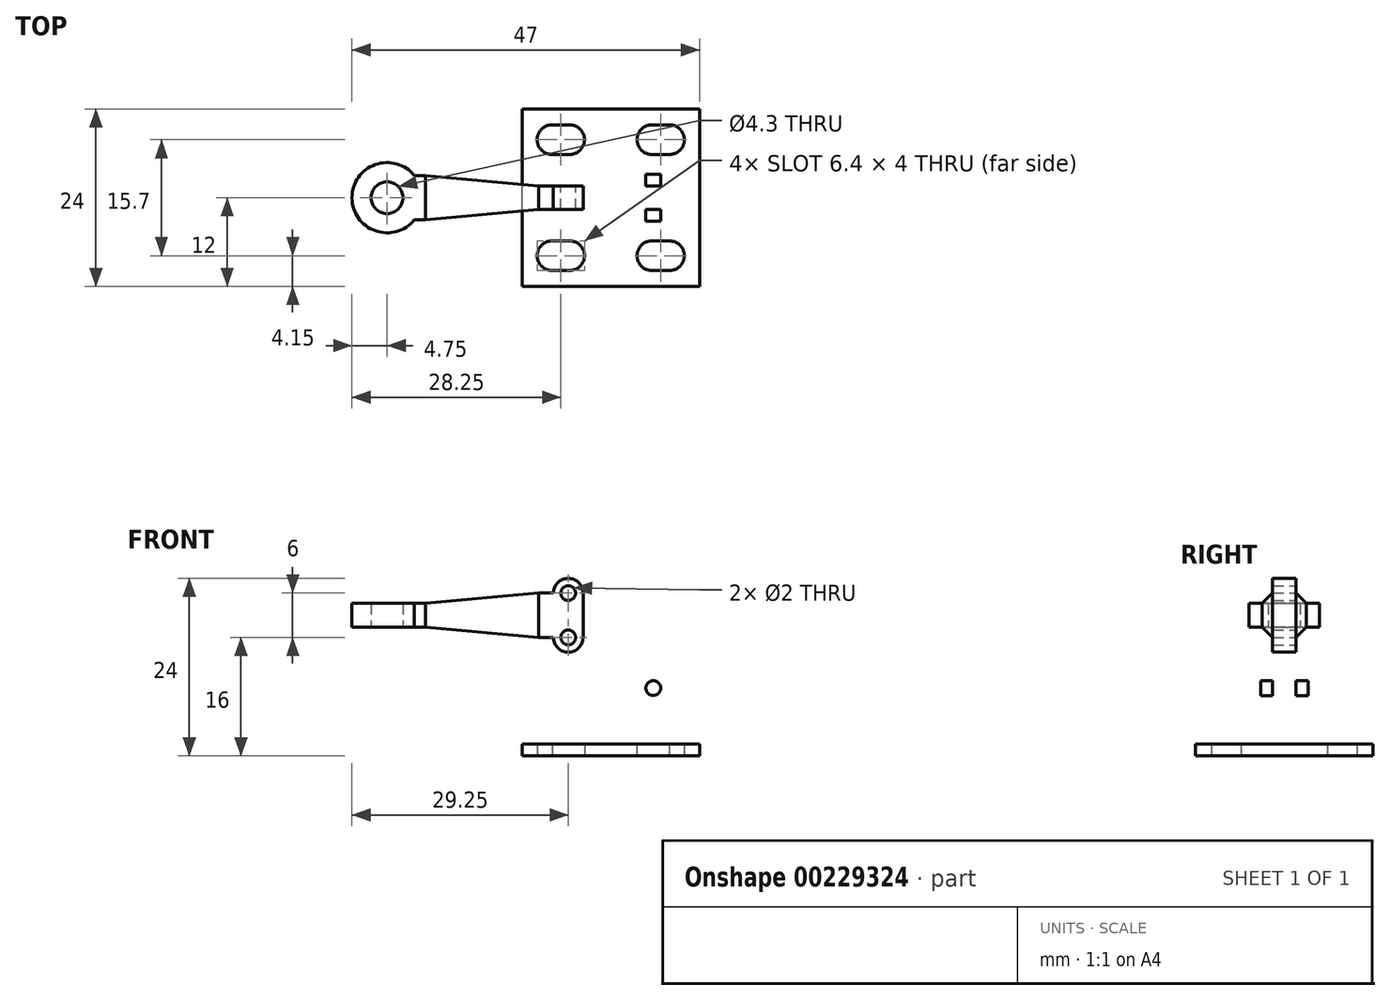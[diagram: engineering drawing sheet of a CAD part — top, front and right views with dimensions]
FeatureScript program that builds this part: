
annotation { "Feature Type Name" : "Feature", "Feature Type Description" : "" }
export const myFeature = defineFeature(function(context is Context, id is Id, definition is map)
    precondition{}
    {
        {
            var Q0;
            Q0=qCreatedBy(makeId("Top.planeOp"),FACE);
            var sketch = newSketch(context, id + "F0", { "sketchPlane" : qUnion([Q0])});
            skLineSegment(sketch, "E0.bottom", {"start": v(12, -12) * mm, "end": v(-12, -12) * mm});
            skLineSegment(sketch, "E0.top", {"start": v(12, 12) * mm, "end": v(-12, 12) * mm});
            skLineSegment(sketch, "E0.left", {"start": v(12, -12) * mm, "end": v(12, 12) * mm});
            skLineSegment(sketch, "E0.right", {"start": v(-12, -12) * mm, "end": v(-12, 12) * mm});
            skPoint(sketch, "E0.middle", {"position": v(0, 0) * mm});
            skArc(sketch, "E1", {"start": v(-5.55, -9.85) * mm, "mid": v(-3.55, -7.85) * mm, "end": v(-5.55, -5.85) * mm});
            skLineSegment(sketch, "E2", {"start": v(-8, -5.85) * mm, "end": v(-5.55, -5.85) * mm});
            skLineSegment(sketch, "E3", {"start": v(-7.95, -9.85) * mm, "end": v(-5.55, -9.85) * mm});
            skArc(sketch, "E4.trimOffspring", {"start": v(-7.9, -5.85) * mm, "mid": v(-9.95, -7.82) * mm, "end": v(-7.95, -9.85) * mm});
            skLineSegment(sketch, "E5.MirrorCS", {"start": v(8, -5.85) * mm, "end": v(5.55, -5.85) * mm});
            skLineSegment(sketch, "E6.MirrorCS", {"start": v(7.95, -9.85) * mm, "end": v(5.55, -9.85) * mm});
            skArc(sketch, "E7.MirrorCS", {"start": v(5.55, -9.85) * mm, "mid": v(3.55, -7.85) * mm, "end": v(5.55, -5.85) * mm});
            skArc(sketch, "E8.MirrorCS", {"start": v(7.9, -5.85) * mm, "mid": v(9.95, -7.82) * mm, "end": v(7.95, -9.85) * mm});
            skLineSegment(sketch, "E9.MirrorCS", {"start": v(-8, 5.85) * mm, "end": v(-5.55, 5.85) * mm});
            skLineSegment(sketch, "E10.MirrorCS", {"start": v(-7.95, 9.85) * mm, "end": v(-5.55, 9.85) * mm});
            skArc(sketch, "E11.MirrorCS", {"start": v(-7.9, 5.85) * mm, "mid": v(-9.95, 7.82) * mm, "end": v(-7.95, 9.85) * mm});
            skArc(sketch, "E12.MirrorCS", {"start": v(-5.55, 9.85) * mm, "mid": v(-3.55, 7.85) * mm, "end": v(-5.55, 5.85) * mm});
            skArc(sketch, "E13.MirrorCS", {"start": v(5.55, 9.85) * mm, "mid": v(3.55, 7.85) * mm, "end": v(5.55, 5.85) * mm});
            skArc(sketch, "E14.MirrorCS", {"start": v(7.9, 5.85) * mm, "mid": v(9.95, 7.82) * mm, "end": v(7.95, 9.85) * mm});
            skLineSegment(sketch, "E15.MirrorCS", {"start": v(8, 5.85) * mm, "end": v(5.55, 5.85) * mm});
            skLineSegment(sketch, "E16.MirrorCS", {"start": v(7.95, 9.85) * mm, "end": v(5.55, 9.85) * mm});
            skSolve(sketch);
        }
        {
            var Q0;
            Q0=makeQuery(id+"F0.imprint","IMPRINT",FACE,{"disambiguationData":[TD([[makeQuery(id+"F0.imprint","IMPRINT",EDGE,{"derivedFrom":sQuery(id+"F0.wireOp",EDGE,"E0.bottom")}),-1.0]])]});
            extrude(context, id + "F1", {"entities" : qUnion([Q0]), "depth" : 1.6 * mm});
        }
        {
            var Q0;
            Q0=makeQuery(id+"F1.opExtrude","CAP_FACE",FACE,{"disambiguationData":[OSD([sQuery(id+"F0.wireOp",EDGE,"E0.bottom"),sQuery(id+"F0.wireOp",EDGE,"E0.top"),sQuery(id+"F0.wireOp",EDGE,"E0.left"),sQuery(id+"F0.wireOp",EDGE,"E0.right"),sQuery(id+"F0.wireOp",EDGE,"E1"),sQuery(id+"F0.wireOp",EDGE,"E2"),sQuery(id+"F0.wireOp",EDGE,"E3"),sQuery(id+"F0.wireOp",EDGE,"E4.trimOffspring"),sQuery(id+"F0.wireOp",EDGE,"E5.MirrorCS"),sQuery(id+"F0.wireOp",EDGE,"E6.MirrorCS"),sQuery(id+"F0.wireOp",EDGE,"E7.MirrorCS"),sQuery(id+"F0.wireOp",EDGE,"E8.MirrorCS"),sQuery(id+"F0.wireOp",EDGE,"E9.MirrorCS"),sQuery(id+"F0.wireOp",EDGE,"E10.MirrorCS"),sQuery(id+"F0.wireOp",EDGE,"E11.MirrorCS"),sQuery(id+"F0.wireOp",EDGE,"E12.MirrorCS"),sQuery(id+"F0.wireOp",EDGE,"E13.MirrorCS"),sQuery(id+"F0.wireOp",EDGE,"E14.MirrorCS"),sQuery(id+"F0.wireOp",EDGE,"E15.MirrorCS"),sQuery(id+"F0.wireOp",EDGE,"E16.MirrorCS")])],"isStart":false});
            var sketch = newSketch(context, id + "F2", { "sketchPlane" : qUnion([Q0])});
            skLineSegment(sketch, "E17.bottom", {"start": v(12, -3.2) * mm, "end": v(-12, -3.2) * mm});
            skLineSegment(sketch, "E17.top", {"start": v(12, 3.2) * mm, "end": v(-12, 3.2) * mm});
            skLineSegment(sketch, "E17.left", {"start": v(12, -3.2) * mm, "end": v(12, -1.6) * mm});
            skLineSegment(sketch, "E17.right", {"start": v(-12, -3.2) * mm, "end": v(-12, -1.6) * mm});
            skPoint(sketch, "E17.middle", {"position": v(0, 0) * mm});
            skLineSegment(sketch, "E18.bottom", {"start": v(12, -1.6) * mm, "end": v(-12, -1.6) * mm});
            skLineSegment(sketch, "E18.top", {"start": v(12, 1.6) * mm, "end": v(-12, 1.6) * mm});
            skLineSegment(sketch, "E19.trimOffspring", {"start": v(-12, 1.6) * mm, "end": v(-12, 3.2) * mm});
            skLineSegment(sketch, "E20.trimOffspring", {"start": v(12, 1.6) * mm, "end": v(12, 3.2) * mm});
            skSolve(sketch);
        }
        {
            var Q0;
            Q0 = qSketchRegion(id + "F2", true);
            extrude(context, id + "F3", {"entities" : qUnion([Q0]), "operationType" : NewBodyOperationType.ADD, "depth" : 15.5 * mm});
        }
        {
            var Q0;
            Q0=makeQuery(id+"F3.opExtrude","SWEPT_FACE",FACE,{"disambiguationData":[OSD([sQuery(id+"F2.wireOp",EDGE,"E17.bottom")])]});
            var sketch = newSketch(context, id + "F4", { "sketchPlane" : qUnion([Q0])});
            skCircle(sketch, "E21", {"center": v(-5.75, 9.15) * mm, "radius": 1 * mm});
            skArc(sketch, "E22", {"start": v(-4.01, 10.14) * mm, "mid": v(-5.78, 11.15) * mm, "end": v(-7.52, 10.08) * mm});
            skArc(sketch, "E23.MirrorC", {"start": v(4.01, 10.14) * mm, "mid": v(5.78, 11.15) * mm, "end": v(7.52, 10.08) * mm});
            skCircle(sketch, "E24.MirrorC", {"center": v(5.75, 9.15) * mm, "radius": 1 * mm});
            skArc(sketch, "E25", {"start": v(-2.6, 7.67) * mm, "mid": v(0, 6.15) * mm, "end": v(2.6, 7.67) * mm});
            skLineSegment(sketch, "E26", {"start": v(12, 1.6) * mm, "end": v(7.52, 10.08) * mm});
            skLineSegment(sketch, "E27", {"start": v(-12, 1.6) * mm, "end": v(-7.52, 10.08) * mm});
            skLineSegment(sketch, "E28", {"start": v(-4.01, 10.14) * mm, "end": v(-2.6, 7.67) * mm});
            skLineSegment(sketch, "E29", {"start": v(4.01, 10.14) * mm, "end": v(2.6, 7.67) * mm});
            skSolve(sketch);
        }
        {
            var Q0;
            Q0=makeQuery(id+"F4.imprint","IMPRINT",FACE,{"disambiguationData":[TD([[makeQuery(id+"F4.imprint","IMPRINT",EDGE,{"derivedFrom":sQuery(id+"F4.wireOp",EDGE,"E22")}),-1.0]])]});
            var Q1;
            Q1=makeQuery(id+"F4.imprint","IMPRINT",FACE,{"disambiguationData":[TD([[makeQuery(id+"F4.imprint","IMPRINT",EDGE,{"derivedFrom":sQuery(id+"F4.wireOp",EDGE,"E24.MirrorC")}),-1.0]])]});
            var Q2;
            Q2=makeQuery(id+"F4.imprint","IMPRINT",FACE,{"disambiguationData":[TD([[makeQuery(id+"F4.imprint","IMPRINT",EDGE,{"derivedFrom":sQuery(id+"F4.wireOp",EDGE,"E21")}),1.0]])]});
            extrude(context, id + "F5", {"entities" : qUnion([Q0, Q1, Q2]), "operationType" : NewBodyOperationType.REMOVE, "endBound" : BoundingType.THROUGH_ALL, "oppositeDirection" : true, "depth" : 25 * mm});
        }
        {
            var Q0;
            Q0=makeQuery(id+"F3.opExtrude","SWEPT_FACE",FACE,{"disambiguationData":[OSD([sQuery(id+"F2.wireOp",EDGE,"E18.top")])]});
            var sketch = newSketch(context, id + "F6", { "sketchPlane" : qUnion([Q0])});
            skLineSegment(sketch, "E30", {"start": v(-5.75, 9.15) * mm, "end": v(-5.75, 22.85) * mm, "construction": true});
            skArc(sketch, "E31", {"start": v(-7.75, 16) * mm, "mid": v(-5.75, 14) * mm, "end": v(-3.75, 16) * mm});
            skArc(sketch, "E32", {"start": v(-3.75, 22) * mm, "mid": v(-5.75, 24) * mm, "end": v(-7.75, 22) * mm});
            skCircle(sketch, "E33", {"center": v(-5.75, 22) * mm, "radius": 1 * mm});
            skCircle(sketch, "E34", {"center": v(-5.75, 16) * mm, "radius": 1 * mm});
            skLineSegment(sketch, "E35", {"start": v(-5.75, 22) * mm, "end": v(-9.75, 22) * mm});
            skLineSegment(sketch, "E36", {"start": v(-9.75, 22) * mm, "end": v(-9.75, 16) * mm});
            skLineSegment(sketch, "E37", {"start": v(-9.75, 16) * mm, "end": v(-5.75, 16) * mm});
            skLineSegment(sketch, "E38", {"start": v(-3.75, 22) * mm, "end": v(-3.75, 16) * mm});
            skSolve(sketch);
        }
        {
            var Q0;
            Q0 = qSketchRegion(id + "F6", true);
            extrude(context, id + "F7", {"entities" : qUnion([Q0]), "depth" : 3.2 * mm});
        }
        {
            var Q0;
            Q0=qCreatedBy(makeId("Top.planeOp"),FACE);
            cPlane(context, id + "F8", {"entities" : qUnion([Q0]), "cplaneType" : CPlaneType.OFFSET, "offset" : 19 * mm, "width" : 150 * mm, "height" : 150 * mm});
        }
        {
            var Q0;
            Q0=qCreatedBy(id+"F8.planeOp",FACE);
            var sketch = newSketch(context, id + "F9", { "sketchPlane" : qUnion([Q0])});
            skArc(sketch, "E39", {"start": v(-26.57, 3) * mm, "mid": v(-35, 0) * mm, "end": v(-26.57, -3) * mm});
            skCircle(sketch, "E40", {"center": v(-30.25, 0) * mm, "radius": 2.15 * mm});
            skLineSegment(sketch, "E41.bottom", {"start": v(-25.07, -3) * mm, "end": v(-26.57, -3) * mm});
            skLineSegment(sketch, "E41.top", {"start": v(-25.07, 3) * mm, "end": v(-26.57, 3) * mm});
            skLineSegment(sketch, "E41.left", {"start": v(-25.07, -3) * mm, "end": v(-25.07, 3) * mm});
            skPoint(sketch, "E41.middle", {"position": v(-25.82, 0) * mm});
            skSolve(sketch);
        }
        {
            var Q0;
            Q0 = qSketchRegion(id + "F9", true);
            extrude(context, id + "F10", {"entities" : qUnion([Q0]), "endBound" : BoundingType.SYMMETRIC, "depth" : 3.2 * mm});
        }
        {
            var Q0;
            Q0=makeQuery(id+"F10.opExtrude","SWEPT_FACE",FACE,{"disambiguationData":[OSD([sQuery(id+"F9.wireOp",EDGE,"E41.left")])]});
            var Q1;
            Q1=makeQuery(id+"F7.opExtrude","SWEPT_FACE",FACE,{"disambiguationData":[OSD([sQuery(id+"F6.wireOp",EDGE,"E36")])]});
            loft(context, id + "F11", {"sheetProfilesArray" : [{ "sheetProfileEntities" : qUnion([Q0]) }, { "sheetProfileEntities" : qUnion([Q1]) }]});
        }
    });
